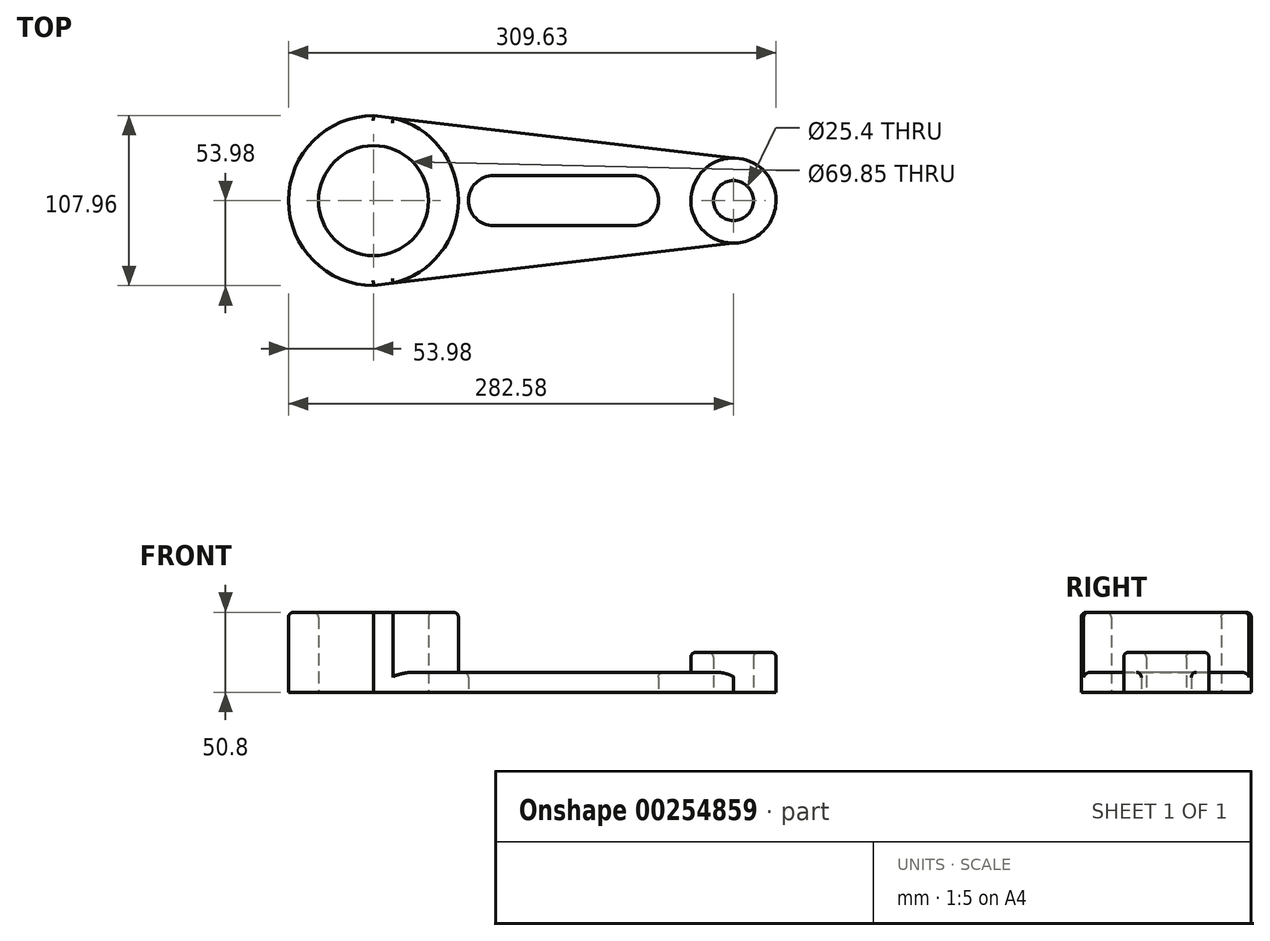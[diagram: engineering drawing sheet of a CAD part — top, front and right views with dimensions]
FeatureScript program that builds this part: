
annotation { "Feature Type Name" : "Feature", "Feature Type Description" : "" }
export const myFeature = defineFeature(function(context is Context, id is Id, definition is map)
    precondition{}
    {
        {
            var Q0;
            Q0=qCreatedBy(makeId("Top.planeOp"),FACE);
            var sketch = newSketch(context, id + "F0", { "sketchPlane" : qUnion([Q0])});
            skCircle(sketch, "E0", {"center": v(-76.2, 0) * mm, "radius": 34.93 * mm});
            skCircle(sketch, "E1", {"center": v(-76.2, 0) * mm, "radius": 53.98 * mm});
            skCircle(sketch, "E2", {"center": v(152.4, 0) * mm, "radius": 12.7 * mm});
            skCircle(sketch, "E3", {"center": v(152.4, 0) * mm, "radius": 27.05 * mm});
            skLineSegment(sketch, "E4", {"start": v(-76.2, 53.98) * mm, "end": v(152.4, 27.05) * mm});
            skLineSegment(sketch, "E5", {"start": v(-76.2, -53.98) * mm, "end": v(152.4, -27.05) * mm});
            skCircle(sketch, "E6", {"center": v(0, 0) * mm, "radius": 15.88 * mm});
            skCircle(sketch, "E7", {"center": v(88.9, 0) * mm, "radius": 15.88 * mm});
            skLineSegment(sketch, "E8", {"start": v(0, 15.88) * mm, "end": v(88.9, 15.88) * mm});
            skLineSegment(sketch, "E9", {"start": v(0, -15.88) * mm, "end": v(88.9, -15.88) * mm});
            skSolve(sketch);
        }
        {
            var Q0;
            Q0=makeQuery(id+"F0.imprint","IMPRINT",FACE,{"disambiguationData":[TD([[makeQuery(id+"F0.imprint","IMPRINT",EDGE,{"derivedFrom":sQuery(id+"F0.wireOp",EDGE,"E0")}),-1.0]])]});
            var Q1;
            Q1=makeQuery(id+"F0.imprint","IMPRINT",FACE,{"disambiguationData":[TD([[makeQuery(id+"F0.imprint","IMPRINT",EDGE,{"derivedFrom":sQuery(id+"F0.wireOp",EDGE,"E2")}),-1.0]])]});
            var Q2;
            {var subQ9=sQuery(id+"F0.wireOp",EDGE,"E8");Q2=makeQuery(id+"F0.imprint","IMPRINT",FACE,{"disambiguationData":[TD([[makeQuery(id+"F0.imprint","IMPRINT",EDGE,{"derivedFrom":subQ9}),1.0]])]});}
            extrude(context, id + "F1", {"entities" : qUnion([Q0, Q1, Q2]), "depth" : 12.7 * mm});
        }
        {
            var Q0;
            Q0=makeQuery(id+"F1.opExtrude","CAP_FACE",FACE,{"disambiguationData":[OSD([sQuery(id+"F0.wireOp",EDGE,"E0"),sQuery(id+"F0.wireOp",EDGE,"E1"),sQuery(id+"F0.wireOp",EDGE,"E2"),sQuery(id+"F0.wireOp",EDGE,"E3"),sQuery(id+"F0.wireOp",EDGE,"E4"),sQuery(id+"F0.wireOp",EDGE,"E5"),sQuery(id+"F0.wireOp",EDGE,"E6"),sQuery(id+"F0.wireOp",EDGE,"E7"),sQuery(id+"F0.wireOp",EDGE,"E8"),sQuery(id+"F0.wireOp",EDGE,"E9")])],"isStart":false});
            var sketch = newSketch(context, id + "F2", { "sketchPlane" : qUnion([Q0])});
            skCircle(sketch, "E10", {"center": v(-76.2, 0) * mm, "radius": 53.98 * mm});
            skCircle(sketch, "E11", {"center": v(152.4, 0) * mm, "radius": 27.05 * mm});
            skSolve(sketch);
        }
        {
            var Q0;
            Q0=makeQuery(id+"F2.imprint","IMPRINT",FACE,{"disambiguationData":[TD([[makeQuery(id+"F2.imprint","IMPRINT",EDGE,{"derivedFrom":makeQuery(id+"F1.opExtrude","CAP_EDGE",EDGE,{"disambiguationData":[OSD([sQuery(id+"F0.wireOp",EDGE,"E0")])],"isStart":false})}),-1.0]])]});
            extrude(context, id + "F3", {"entities" : qUnion([Q0]), "operationType" : NewBodyOperationType.ADD, "depth" : 38.1 * mm});
        }
        {
            var Q0;
            Q0=makeQuery(id+"F1.opExtrude","CAP_FACE",FACE,{"disambiguationData":[OSD([sQuery(id+"F0.wireOp",EDGE,"E0"),sQuery(id+"F0.wireOp",EDGE,"E1"),sQuery(id+"F0.wireOp",EDGE,"E2"),sQuery(id+"F0.wireOp",EDGE,"E3"),sQuery(id+"F0.wireOp",EDGE,"E4"),sQuery(id+"F0.wireOp",EDGE,"E5"),sQuery(id+"F0.wireOp",EDGE,"E6"),sQuery(id+"F0.wireOp",EDGE,"E7"),sQuery(id+"F0.wireOp",EDGE,"E8"),sQuery(id+"F0.wireOp",EDGE,"E9")])],"isStart":false});
            var sketch = newSketch(context, id + "F4", { "sketchPlane" : qUnion([Q0])});
            skCircle(sketch, "E12", {"center": v(152.4, 0) * mm, "radius": 27.05 * mm});
            skSolve(sketch);
        }
        {
            var Q0;
            Q0=makeQuery(id+"F4.imprint","IMPRINT",FACE,{"disambiguationData":[TD([[makeQuery(id+"F4.imprint","IMPRINT",EDGE,{"derivedFrom":makeQuery(id+"F1.opExtrude","CAP_EDGE",EDGE,{"disambiguationData":[OSD([sQuery(id+"F0.wireOp",EDGE,"E2")])],"isStart":false})}),-1.0]])]});
            extrude(context, id + "F5", {"entities" : qUnion([Q0]), "operationType" : NewBodyOperationType.ADD, "depth" : 12.7 * mm});
        }
        {
            var Q0;
            Q0=makeQuery(id+"F1.opExtrude","CAP_EDGE",EDGE,{"disambiguationData":[OSD([sQuery(id+"F0.wireOp",EDGE,"E5")])],"isStart":false});
            var Q1;
            Q1=makeQuery(id+"F1.opExtrude","CAP_EDGE",EDGE,{"disambiguationData":[OSD([sQuery(id+"F0.wireOp",EDGE,"E4")])],"isStart":false});
            var Q2;
            Q2=makeQuery(id+"F5.opExtrude","CAP_EDGE",EDGE,{"disambiguationData":[OSD([sQuery(id+"F4.wireOp",EDGE,"E12")])],"isStart":false});
            var Q3;
            Q3=makeQuery(id+"F5.opExtrude","CAP_EDGE",EDGE,{"disambiguationData":[OSD([sQuery(id+"F0.wireOp",EDGE,"E2")])],"isStart":false});
            var Q4;
            {var subQ0=sQuery(id+"F2.wireOp",EDGE,"E10");Q4=makeQuery(id+"F3.opExtrude","CAP_EDGE",EDGE,{"disambiguationData":[OSD([subQ0]),TDD([makeQuery(id+"F2.imprint","IMPRINT",EDGE,{"disambiguationData":[TD([[makeQuery(id+"F2.imprint","INTERSECT",VERTEX,{"disambiguationData":[OD(1.0)],"derivedFrom":[makeQuery(id+"F1.opExtrude","CAP_EDGE",EDGE,{"disambiguationData":[OSD([sQuery(id+"F0.wireOp",EDGE,"E4")])],"isStart":false}),subQ0]}),1.0]])],"derivedFrom":subQ0})])],"isStart":false});}
            var Q5;
            {var subQ0=sQuery(id+"F2.wireOp",EDGE,"E10");Q5=makeQuery(id+"F3.opExtrude","CAP_EDGE",EDGE,{"disambiguationData":[OSD([subQ0]),TDD([makeQuery(id+"F2.imprint","IMPRINT",EDGE,{"disambiguationData":[TD([[makeQuery(id+"F2.imprint","INTERSECT",VERTEX,{"disambiguationData":[OD(0.0)],"derivedFrom":[makeQuery(id+"F1.opExtrude","CAP_EDGE",EDGE,{"disambiguationData":[OSD([sQuery(id+"F0.wireOp",EDGE,"E4")])],"isStart":false}),subQ0]}),-1.0]])],"derivedFrom":subQ0})])],"isStart":false});}
            var Q6;
            Q6=makeQuery(id+"F3.opExtrude","CAP_EDGE",EDGE,{"disambiguationData":[OSD([sQuery(id+"F0.wireOp",EDGE,"E4")])],"isStart":false});
            var Q7;
            Q7=makeQuery(id+"F3.opExtrude","CAP_EDGE",EDGE,{"disambiguationData":[OSD([sQuery(id+"F0.wireOp",EDGE,"E5")])],"isStart":false});
            var Q8;
            Q8=makeQuery(id+"F3.opExtrude","CAP_EDGE",EDGE,{"disambiguationData":[OSD([sQuery(id+"F0.wireOp",EDGE,"E0")])],"isStart":false});
            fillet(context, id + "F6", {"entities" : qUnion([Q0, Q1, Q2, Q3, Q4, Q5, Q6, Q7, Q8]), "radius" : 3.17 * mm, "tangentPropagation" : true, "allowEdgeOverflow" : false});
        }
        {
            var Q0;
            Q0=makeQuery(id+"F1.opExtrude","CAP_EDGE",EDGE,{"disambiguationData":[OSD([sQuery(id+"F0.wireOp",EDGE,"E8")])],"isStart":false});
            var Q1;
            Q1=makeQuery(id+"F1.opExtrude","CAP_EDGE",EDGE,{"disambiguationData":[OSD([sQuery(id+"F0.wireOp",EDGE,"E6")])],"isStart":false});
            var Q2;
            Q2=makeQuery(id+"F1.opExtrude","CAP_EDGE",EDGE,{"disambiguationData":[OSD([sQuery(id+"F0.wireOp",EDGE,"E9")])],"isStart":false});
            var Q3;
            Q3=makeQuery(id+"F1.opExtrude","CAP_EDGE",EDGE,{"disambiguationData":[OSD([sQuery(id+"F0.wireOp",EDGE,"E7")])],"isStart":false});
            fillet(context, id + "F7", {"entities" : qUnion([Q0, Q1, Q2, Q3]), "radius" : 3.17 * mm, "tangentPropagation" : true, "allowEdgeOverflow" : false});
        }
    });
